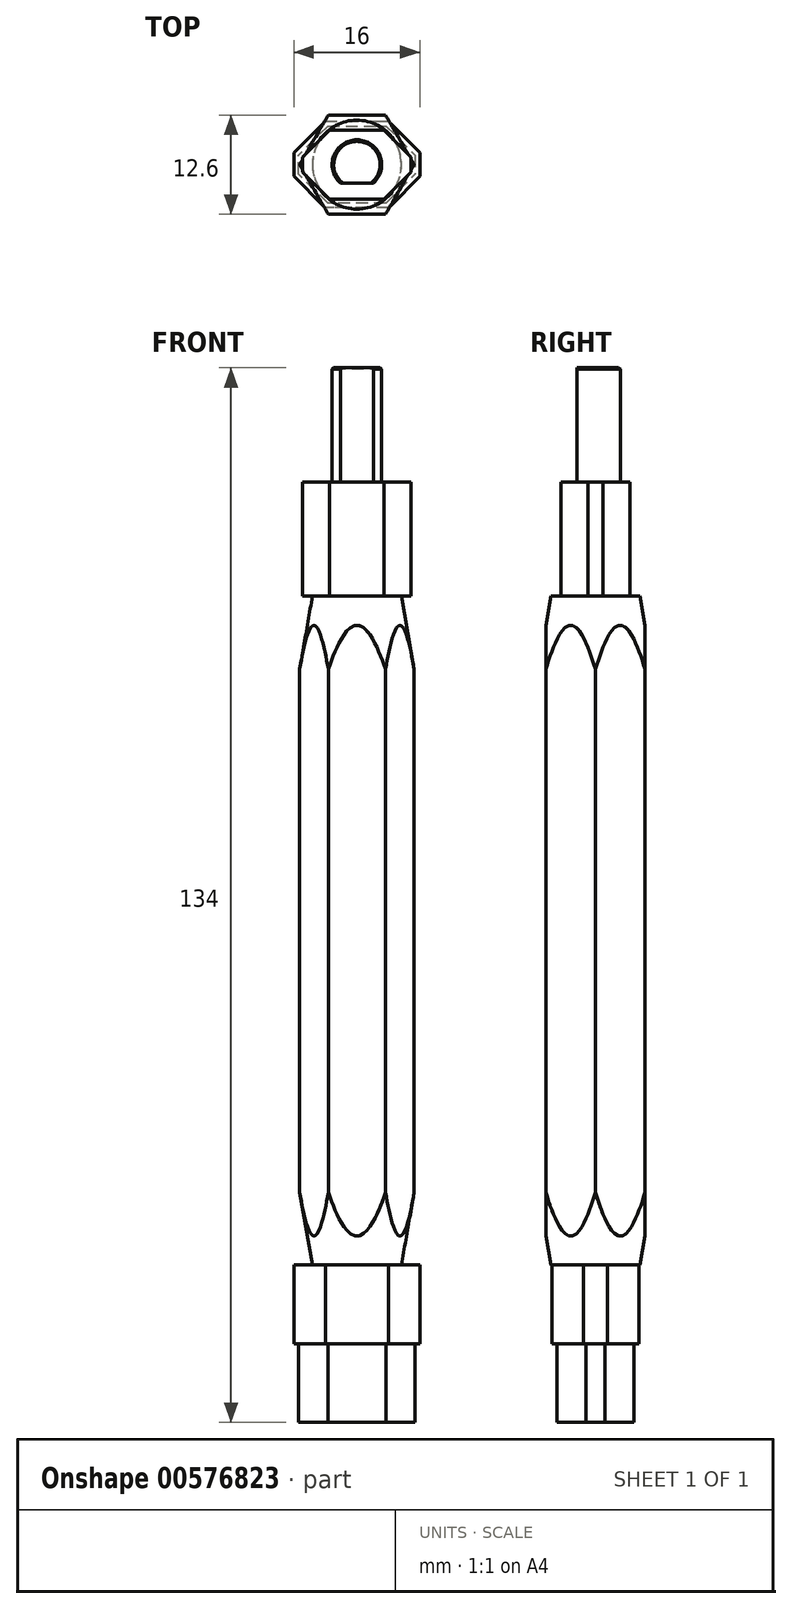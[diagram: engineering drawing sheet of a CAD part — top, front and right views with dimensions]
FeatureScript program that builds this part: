
annotation { "Feature Type Name" : "Feature", "Feature Type Description" : "" }
export const myFeature = defineFeature(function(context is Context, id is Id, definition is map)
    precondition{}
    {
        {
            var Q0;
            Q0=qCreatedBy(makeId("Top.planeOp"),FACE);
            var sketch = newSketch(context, id + "F0", { "sketchPlane" : qUnion([Q0])});
            skLineSegment(sketch, "E0", {"start": v(0, 0) * mm, "end": v(0, -4.4) * mm});
            skLineSegment(sketch, "E1", {"start": v(0, -4.4) * mm, "end": v(3.45, -4.4) * mm});
            skLineSegment(sketch, "E2", {"start": v(6.9, -0.95) * mm, "end": v(6.9, 0.95) * mm});
            skLineSegment(sketch, "E3", {"start": v(3.45, 4.4) * mm, "end": v(-3.45, 4.4) * mm});
            skLineSegment(sketch, "E4", {"start": v(-6.9, 0.95) * mm, "end": v(-6.9, -0.95) * mm});
            skLineSegment(sketch, "E5", {"start": v(-3.45, -4.4) * mm, "end": v(0, -4.4) * mm});
            skLineSegment(sketch, "E6", {"start": v(-3.45, -4.4) * mm, "end": v(-6.9, -0.95) * mm});
            skLineSegment(sketch, "E7", {"start": v(3.45, -4.4) * mm, "end": v(6.9, -0.95) * mm});
            skPoint(sketch, "E8.orphan", {"position": v(-6.9, -4.4) * mm});
            skPoint(sketch, "E9.orphan", {"position": v(6.9, -4.4) * mm});
            skLineSegment(sketch, "E10", {"start": v(-3.45, 4.4) * mm, "end": v(-6.9, 0.95) * mm});
            skLineSegment(sketch, "E11", {"start": v(6.9, 0.95) * mm, "end": v(3.45, 4.4) * mm});
            skSolve(sketch);
        }
        {
            var Q0;
            Q0 = qSketchRegion(id + "F0", true);
            extrude(context, id + "F1", {"entities" : qUnion([Q0]), "depth" : 14.5 * mm, "offsetDistance" : 25 * mm});
        }
        {
            var Q0;
            Q0=makeQuery(id+"F1.opExtrude","CAP_FACE",FACE,{"disambiguationData":[OSD([sQuery(id+"F0.wireOp",EDGE,"E1"),sQuery(id+"F0.wireOp",EDGE,"E2"),sQuery(id+"F0.wireOp",EDGE,"E3"),sQuery(id+"F0.wireOp",EDGE,"E4"),sQuery(id+"F0.wireOp",EDGE,"E5"),sQuery(id+"F0.wireOp",EDGE,"E6"),sQuery(id+"F0.wireOp",EDGE,"E7"),sQuery(id+"F0.wireOp",EDGE,"E10"),sQuery(id+"F0.wireOp",EDGE,"E11")])],"isStart":false});
            var sketch = newSketch(context, id + "F2", { "sketchPlane" : qUnion([Q0])});
            skCircle(sketch, "E12", {"center": v(0, 0) * mm, "radius": 3.15 * mm});
            skSolve(sketch);
        }
        {
            var Q0;
            Q0 = qSketchRegion(id + "F2", true);
            extrude(context, id + "F3", {"entities" : qUnion([Q0]), "operationType" : NewBodyOperationType.ADD, "depth" : 14.5 * mm, "offsetDistance" : 25 * mm});
        }
        {
            var Q0;
            Q0=makeQuery(id+"F3.opExtrude","CAP_EDGE",EDGE,{"disambiguationData":[OSD([sQuery(id+"F2.wireOp",EDGE,"E12")])],"isStart":false});
            chamfer(context, id + "F4", {"entities" : qUnion([Q0]), "width" : .2 * mm, "tangentPropagation" : true});
        }
        {
            var Q0;
            Q0=makeQuery(id+"F3.opExtrude","CAP_FACE",FACE,{"disambiguationData":[OSD([sQuery(id+"F2.wireOp",EDGE,"E12")])],"isStart":false});
            var sketch = newSketch(context, id + "F5", { "sketchPlane" : qUnion([Q0])});
            skLineSegment(sketch, "E13", {"start": v(0, 0) * mm, "end": v(0, -3.15) * mm});
            skLineSegment(sketch, "E14", {"start": v(0, -3.15) * mm, "end": v(0, -2.35) * mm});
            skLineSegment(sketch, "E15", {"start": v(0, -2.35) * mm, "end": v(-2.5, -2.35) * mm});
            skLineSegment(sketch, "E16", {"start": v(-2.5, -2.35) * mm, "end": v(3.29, -2.35) * mm});
            skLineSegment(sketch, "E17", {"start": v(3.29, -2.35) * mm, "end": v(3.29, -3.15) * mm});
            skLineSegment(sketch, "E18", {"start": v(3.29, -3.15) * mm, "end": v(-2.5, -3.15) * mm});
            skLineSegment(sketch, "E19", {"start": v(-2.5, -3.15) * mm, "end": v(-2.5, -2.35) * mm});
            skSolve(sketch);
        }
        {
            var Q0;
            Q0 = qSketchRegion(id + "F5", true);
            extrude(context, id + "F6", {"entities" : qUnion([Q0]), "operationType" : NewBodyOperationType.REMOVE, "oppositeDirection" : true, "depth" : 14.5 * mm, "offsetDistance" : 25 * mm});
        }
        {
            var Q0;
            Q0=makeQuery(id+"F1.opExtrude","CAP_FACE",FACE,{"disambiguationData":[OSD([sQuery(id+"F0.wireOp",EDGE,"E1"),sQuery(id+"F0.wireOp",EDGE,"E2"),sQuery(id+"F0.wireOp",EDGE,"E3"),sQuery(id+"F0.wireOp",EDGE,"E4"),sQuery(id+"F0.wireOp",EDGE,"E5"),sQuery(id+"F0.wireOp",EDGE,"E6"),sQuery(id+"F0.wireOp",EDGE,"E7"),sQuery(id+"F0.wireOp",EDGE,"E10"),sQuery(id+"F0.wireOp",EDGE,"E11")])],"isStart":true});
            var sketch = newSketch(context, id + "F7", { "sketchPlane" : qUnion([Q0])});
            skCircle(sketch, "E20.cCircle", {"center": v(0, 0) * mm, "radius": 7.27 * mm, "construction": true});
            skLineSegment(sketch, "E20.0", {"start": v(7.27, 0) * mm, "end": v(3.64, -6.3) * mm});
            skLineSegment(sketch, "E20.1", {"start": v(3.64, -6.3) * mm, "end": v(-3.64, -6.3) * mm});
            skLineSegment(sketch, "E20.2", {"start": v(-3.64, -6.3) * mm, "end": v(-7.27, 0) * mm});
            skLineSegment(sketch, "E20.3", {"start": v(-7.27, 0) * mm, "end": v(-3.64, 6.3) * mm});
            skLineSegment(sketch, "E20.4", {"start": v(-3.64, 6.3) * mm, "end": v(3.64, 6.3) * mm});
            skLineSegment(sketch, "E20.5", {"start": v(3.64, 6.3) * mm, "end": v(7.27, 0) * mm});
            skSolve(sketch);
        }
        {
            var Q0;
            Q0 = qSketchRegion(id + "F7", true);
            extrude(context, id + "F8", {"entities" : qUnion([Q0]), "operationType" : NewBodyOperationType.ADD, "depth" : 85 * mm, "offsetDistance" : 25 * mm});
        }
        {
            var Q0;
            {var subQ0=sQuery(id+"F0.wireOp",EDGE,"E6");var subQ4=sQuery(id+"F7.wireOp",EDGE,"E20.5");var subQ5=sQuery(id+"F7.wireOp",EDGE,"E20.3");var subQ6=sQuery(id+"F7.wireOp",EDGE,"E20.4");Q0=makeQuery(id+"F8.boolean.opBoolean","SPLIT",FACE,{"disambiguationData":[TD([makeQuery(id+"F1.opExtrude","SWEPT_FACE",FACE,{"disambiguationData":[OSD([subQ0])]})])],"derivedFrom":makeQuery(id+"F8.opExtrude","CAP_FACE",FACE,{"disambiguationData":[OSD([sQuery(id+"F7.wireOp",EDGE,"E20.0"),sQuery(id+"F7.wireOp",EDGE,"E20.1"),sQuery(id+"F7.wireOp",EDGE,"E20.2"),subQ5,subQ6,subQ4])],"isStart":true})});}
            var sketch = newSketch(context, id + "F9", { "sketchPlane" : qUnion([Q0])});
            skCircle(sketch, "E21", {"center": v(0, 0) * mm, "radius": 5.65 * mm});
            skCircle(sketch, "E22", {"center": v(0, 0) * mm, "radius": 16.14 * mm});
            skSolve(sketch);
        }
        {
            var Q0;
            Q0 = qSketchRegion(id + "F9", true);
            extrude(context, id + "F10", {"entities" : qUnion([Q0]), "operationType" : NewBodyOperationType.REMOVE, "oppositeDirection" : true, "depth" : 10 * mm, "offsetDistance" : 25 * mm, "hasDraft" : true, "draftAngle" : 9.9 * degree, "draftPullDirection" : true});
        }
        {
            var Q0;
            Q0=makeQuery(id+"F8.opExtrude","CAP_FACE",FACE,{"disambiguationData":[OSD([sQuery(id+"F7.wireOp",EDGE,"E20.0"),sQuery(id+"F7.wireOp",EDGE,"E20.1"),sQuery(id+"F7.wireOp",EDGE,"E20.2"),sQuery(id+"F7.wireOp",EDGE,"E20.3"),sQuery(id+"F7.wireOp",EDGE,"E20.4"),sQuery(id+"F7.wireOp",EDGE,"E20.5")])],"isStart":false});
            var sketch = newSketch(context, id + "F11", { "sketchPlane" : qUnion([Q0])});
            skCircle(sketch, "E23", {"center": v(0, 0) * mm, "radius": 17.55 * mm});
            skCircle(sketch, "E24", {"center": v(0, 0) * mm, "radius": 5.65 * mm});
            skSolve(sketch);
        }
        {
            var Q0;
            Q0 = qSketchRegion(id + "F11", true);
            extrude(context, id + "F12", {"entities" : qUnion([Q0]), "operationType" : NewBodyOperationType.REMOVE, "oppositeDirection" : true, "depth" : 25 * mm, "offsetDistance" : 25 * mm, "hasDraft" : true, "draftAngle" : 10 * degree, "draftPullDirection" : true});
        }
        {
            var Q0;
            Q0=makeQuery(id+"F8.opExtrude","CAP_FACE",FACE,{"disambiguationData":[OSD([sQuery(id+"F7.wireOp",EDGE,"E20.0"),sQuery(id+"F7.wireOp",EDGE,"E20.1"),sQuery(id+"F7.wireOp",EDGE,"E20.2"),sQuery(id+"F7.wireOp",EDGE,"E20.3"),sQuery(id+"F7.wireOp",EDGE,"E20.4"),sQuery(id+"F7.wireOp",EDGE,"E20.5")])],"isStart":false});
            var sketch = newSketch(context, id + "F13", { "sketchPlane" : qUnion([Q0])});
            skLineSegment(sketch, "E25", {"start": v(0, 0) * mm, "end": v(0, -5.5) * mm});
            skLineSegment(sketch, "E26", {"start": v(0, -5.5) * mm, "end": v(4, -5.5) * mm});
            skLineSegment(sketch, "E27", {"start": v(8, -1.5) * mm, "end": v(8, 0) * mm});
            skLineSegment(sketch, "E28", {"start": v(8, 0) * mm, "end": v(8, 1.5) * mm});
            skLineSegment(sketch, "E29", {"start": v(4, 5.5) * mm, "end": v(0, 5.5) * mm});
            skLineSegment(sketch, "E30", {"start": v(0, 5.5) * mm, "end": v(-4, 5.5) * mm});
            skLineSegment(sketch, "E31", {"start": v(-8, 1.5) * mm, "end": v(-8, 0) * mm});
            skLineSegment(sketch, "E32", {"start": v(-8, 0) * mm, "end": v(-8, -1.5) * mm});
            skLineSegment(sketch, "E33", {"start": v(-4, -5.5) * mm, "end": v(0, -5.5) * mm});
            skLineSegment(sketch, "E34", {"start": v(-4, -5.5) * mm, "end": v(-8, -1.5) * mm});
            skLineSegment(sketch, "E35", {"start": v(-4, 5.5) * mm, "end": v(-8, 1.5) * mm});
            skLineSegment(sketch, "E36", {"start": v(4, 5.5) * mm, "end": v(8, 1.5) * mm});
            skLineSegment(sketch, "E37", {"start": v(4, -5.5) * mm, "end": v(8, -1.5) * mm});
            skPoint(sketch, "E38.orphan", {"position": v(8, -5.5) * mm});
            skPoint(sketch, "E39.orphan", {"position": v(-8, -5.5) * mm});
            skPoint(sketch, "E40.orphan", {"position": v(-8, 5.5) * mm});
            skPoint(sketch, "E41.orphan", {"position": v(8, 5.5) * mm});
            skSolve(sketch);
        }
        {
            var Q0;
            Q0 = qSketchRegion(id + "F13", true);
            extrude(context, id + "F14", {"entities" : qUnion([Q0]), "operationType" : NewBodyOperationType.ADD, "depth" : 10 * mm, "offsetDistance" : 25 * mm});
        }
        {
            var Q0;
            Q0=makeQuery(id+"F14.opExtrude","CAP_FACE",FACE,{"disambiguationData":[OSD([sQuery(id+"F13.wireOp",EDGE,"E26"),sQuery(id+"F13.wireOp",EDGE,"E27"),sQuery(id+"F13.wireOp",EDGE,"E28"),sQuery(id+"F13.wireOp",EDGE,"E29"),sQuery(id+"F13.wireOp",EDGE,"E30"),sQuery(id+"F13.wireOp",EDGE,"E31"),sQuery(id+"F13.wireOp",EDGE,"E32"),sQuery(id+"F13.wireOp",EDGE,"E33"),sQuery(id+"F13.wireOp",EDGE,"E34"),sQuery(id+"F13.wireOp",EDGE,"E35"),sQuery(id+"F13.wireOp",EDGE,"E36"),sQuery(id+"F13.wireOp",EDGE,"E37")])],"isStart":false});
            var sketch = newSketch(context, id + "F15", { "sketchPlane" : qUnion([Q0])});
            skLineSegment(sketch, "E42", {"start": v(0, 0) * mm, "end": v(0, -4.9) * mm});
            skLineSegment(sketch, "E43", {"start": v(0, -4.9) * mm, "end": v(7.4, -4.9) * mm});
            skLineSegment(sketch, "E44", {"start": v(7.4, -4.9) * mm, "end": v(7.4, 0) * mm});
            skLineSegment(sketch, "E45", {"start": v(7.4, 0) * mm, "end": v(7.4, 4.9) * mm});
            skLineSegment(sketch, "E46", {"start": v(7.4, 4.9) * mm, "end": v(0, 4.9) * mm});
            skLineSegment(sketch, "E47", {"start": v(0, 4.9) * mm, "end": v(-7.4, 4.9) * mm});
            skLineSegment(sketch, "E48", {"start": v(-7.4, 4.9) * mm, "end": v(-7.4, 0) * mm});
            skLineSegment(sketch, "E49", {"start": v(-7.4, 0) * mm, "end": v(-7.4, -4.9) * mm});
            skLineSegment(sketch, "E50", {"start": v(-7.4, -4.9) * mm, "end": v(0, -4.9) * mm});
            skLineSegment(sketch, "E51", {"start": v(3.7, -4.9) * mm, "end": v(7.4, -1.2) * mm});
            skLineSegment(sketch, "E52", {"start": v(3.7, 4.9) * mm, "end": v(7.4, 1.2) * mm});
            skLineSegment(sketch, "E53", {"start": v(-3.7, 4.9) * mm, "end": v(-7.4, 1.2) * mm});
            skLineSegment(sketch, "E54", {"start": v(-3.7, -4.9) * mm, "end": v(-7.4, -1.2) * mm});
            skSolve(sketch);
        }
        {
            var Q0;
            {var subQ1=sQuery(id+"F15.wireOp",EDGE,"E51");Q0=makeQuery(id+"F15.imprint","IMPRINT",FACE,{"disambiguationData":[TD([[makeQuery(id+"F15.imprint","IMPRINT",EDGE,{"derivedFrom":subQ1}),1.0]])]});}
            extrude(context, id + "F16", {"entities" : qUnion([Q0]), "operationType" : NewBodyOperationType.ADD, "depth" : 10 * mm, "offsetDistance" : 25 * mm});
        }
    });
